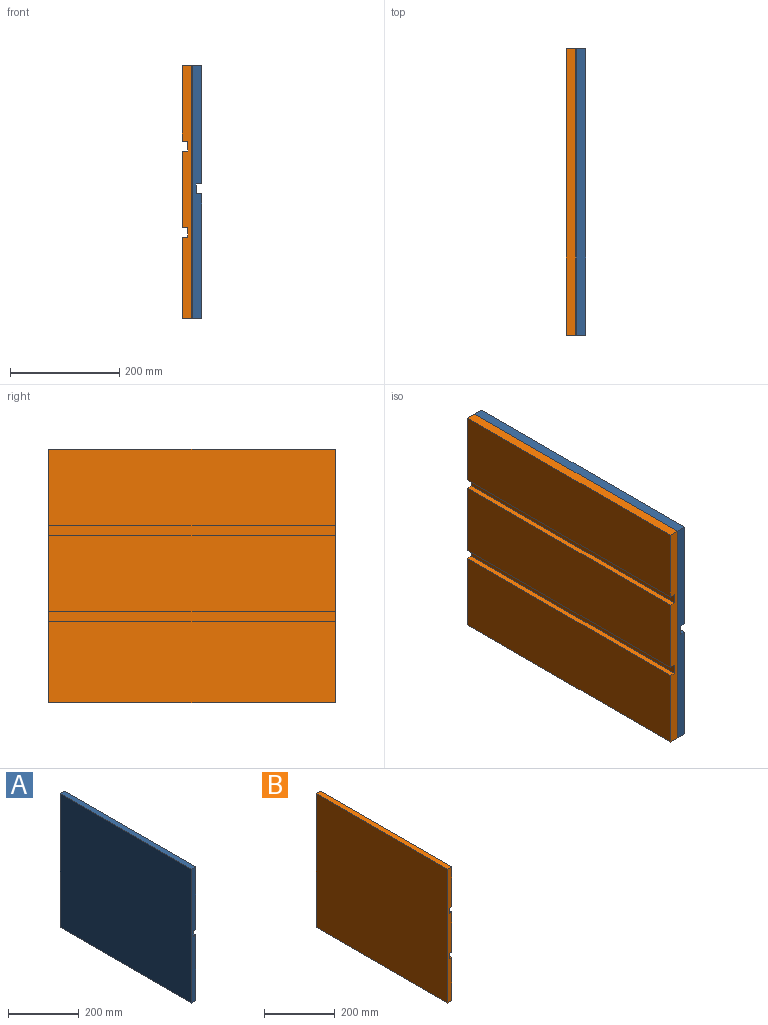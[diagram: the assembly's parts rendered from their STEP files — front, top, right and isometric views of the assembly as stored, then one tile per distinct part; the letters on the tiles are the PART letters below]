
ASSEMBLY  parts=2 mates=1
PART A: 10 faces, bbox 18.3x525.5x463.6 mm
  f0: plane 463.55x18.26mm, normal (0,1,0), area 8274.3mm2, adj f1,f3,f4,f5,f6,f7,f8,f9
  f1: plane 525.46x18.26mm, normal (0,0,1), area 9593mm2, adj f0,f2,f4,f5
  f2: plane 463.55x18.26mm, normal (0,-1,0), area 8274.3mm2, adj f1,f3,f4,f5,f6,f7,f8,f9
  f3: plane 525.46x10.32mm, normal (0,0,-1), area 5422.1mm2, adj f0,f2,f4,f9
  f4: plane 525.46x217.09mm, normal (1,0,0), area 114073mm2, adj f0,f1,f2,f3
  f5: plane 525.46x463.55mm, normal (-1,0,0), area 243578.1mm2, adj f0,f1,f2,f7
  f6: plane 525.46x10.32mm, normal (0,0,1), area 5422.1mm2, adj f0,f2,f8,f9
  f7: plane 525.46x18.26mm, normal (0,0,-1), area 9593mm2, adj f0,f2,f5,f8
  f8: plane 525.46x228.2mm, normal (1,0,0), area 119912.2mm2, adj f0,f2,f6,f7
  f9: plane 525.46x18.26mm, normal (1,0,0), area 9593mm2, adj f0,f2,f3,f6
PART B: 14 faces, bbox 18.3x525.5x463.6 mm
  f0: plane 463.55x18.26mm, normal (0,1,0), area 8085.9mm2, adj f1,f3,f4,f5,f6,f7,f8,f9
  f1: plane 525.46x18.26mm, normal (0,0,1), area 9593mm2, adj f0,f2,f4,f5
  f2: plane 463.55x18.26mm, normal (0,-1,0), area 8085.9mm2, adj f1,f3,f4,f5,f6,f7,f8,f9
  f3: plane 525.46x10.32mm, normal (0,0,-1), area 5422.1mm2, adj f0,f2,f4,f12
  f4: plane 525.46x138.51mm, normal (1,0,0), area 72781.5mm2, adj f0,f1,f2,f3
  f5: plane 525.46x463.55mm, normal (-1,0,0), area 243578.1mm2, adj f0,f1,f2,f7
  f6: plane 525.46x10.32mm, normal (0,0,1), area 5422.1mm2, adj f0,f2,f8,f13
  f7: plane 525.46x18.26mm, normal (0,0,-1), area 9593mm2, adj f0,f2,f5,f8
  f8: plane 525.46x148.83mm, normal (1,0,0), area 78203.6mm2, adj f0,f2,f6,f7
  f9: plane 525.46x10.32mm, normal (0,0,1), area 5422.1mm2, adj f0,f2,f11,f12
  f10: plane 525.46x10.32mm, normal (0,0,-1), area 5422.1mm2, adj f0,f2,f11,f13
  f11: plane 525.46x139.7mm, normal (1,0,0), area 73407.1mm2, adj f0,f2,f9,f10
  f12: plane 525.46x18.26mm, normal (1,0,0), area 9593mm2, adj f0,f2,f3,f9
  f13: plane 525.46x18.26mm, normal (1,0,0), area 9593mm2, adj f0,f2,f6,f10
PLACE A t=(18.26,-341.94,883.01)mm
PLACE B rot(axis=(0,0,-1),180deg) t=(18.26,-341.94,883.01)mm
MATE fastened B.f5 <-> A.f5  axis (1,0,0) through (18.26,0,0)mm
